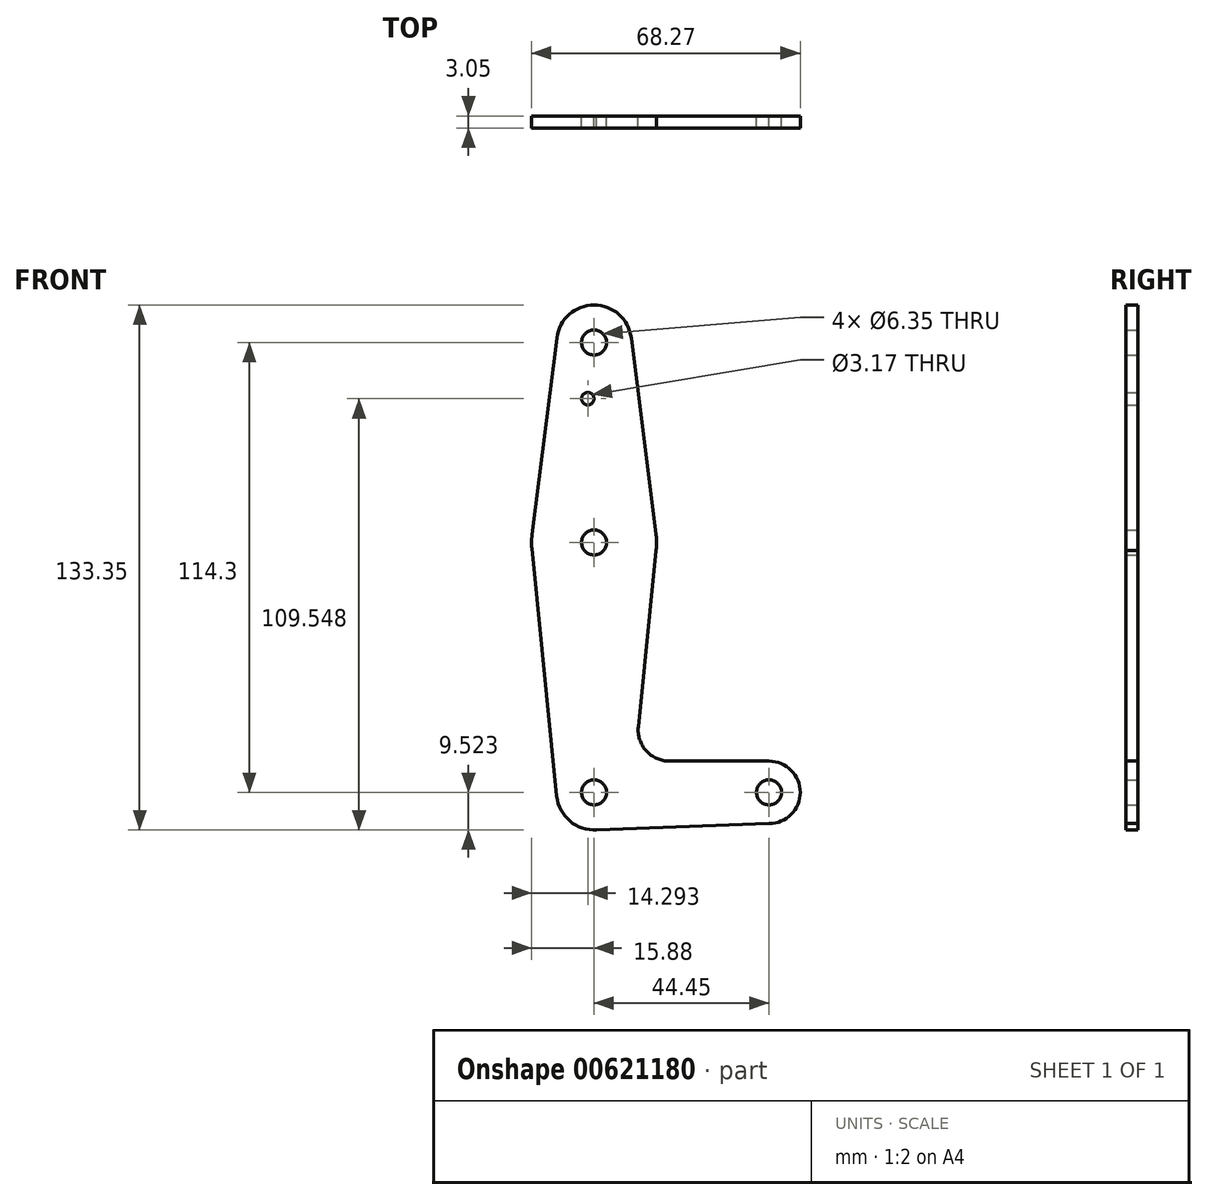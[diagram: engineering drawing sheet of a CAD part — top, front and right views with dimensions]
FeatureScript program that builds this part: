
annotation { "Feature Type Name" : "Feature", "Feature Type Description" : "" }
export const myFeature = defineFeature(function(context is Context, id is Id, definition is map)
    precondition{}
    {
        {
            var Q0;
            Q0=qCreatedBy(makeId("Front.planeOp"),FACE);
            var sketch = newSketch(context, id + "F0", { "sketchPlane" : qUnion([Q0])});
            skCircle(sketch, "E0", {"center": v(0, 85.95) * mm, "radius": 9.53 * mm});
            skCircle(sketch, "E1", {"center": v(0, 35.15) * mm, "radius": 15.88 * mm});
            skCircle(sketch, "E2", {"center": v(0, -28.35) * mm, "radius": 9.53 * mm});
            skCircle(sketch, "E3", {"center": v(44.45, -28.35) * mm, "radius": 7.94 * mm});
            skLineSegment(sketch, "E4", {"start": v(-9.45, 87.14) * mm, "end": v(-15.75, 37.14) * mm});
            skLineSegment(sketch, "E5", {"start": v(15.75, 37.14) * mm, "end": v(9.45, 87.14) * mm});
            skLineSegment(sketch, "E6", {"start": v(15.75, 33.17) * mm, "end": v(11.24, -11.66) * mm});
            skLineSegment(sketch, "E7", {"start": v(19.16, -20.4) * mm, "end": v(44.45, -20.4) * mm});
            skLineSegment(sketch, "E8", {"start": v(0, -37.87) * mm, "end": v(44.45, -36.28) * mm});
            skCircle(sketch, "E9", {"center": v(0, 85.95) * mm, "radius": 3.18 * mm});
            skCircle(sketch, "E10", {"center": v(-1.59, 71.68) * mm, "radius": 1.59 * mm});
            skCircle(sketch, "E11", {"center": v(0, 35.15) * mm, "radius": 3.18 * mm});
            skCircle(sketch, "E12", {"center": v(0, -28.35) * mm, "radius": 3.18 * mm});
            skCircle(sketch, "E13", {"center": v(44.45, -28.35) * mm, "radius": 3.18 * mm});
            skPoint(sketch, "E14.newPointB", {"position": v(9.57, -28.35) * mm});
            skArc(sketch, "E14.filletArc", {"start": v(11.24, -11.66) * mm, "mid": v(13.26, -17.8) * mm, "end": v(19.16, -20.4) * mm});
            skLineSegment(sketch, "E15", {"start": v(0, 85.95) * mm, "end": v(0, 35.15) * mm});
            skLineSegment(sketch, "E16", {"start": v(0, 35.15) * mm, "end": v(0, -18.82) * mm});
            skLineSegment(sketch, "E17", {"start": v(-15.8, 33.57) * mm, "end": v(-9.48, -29.3) * mm});
            skSolve(sketch);
        }
        {
            var Q0;
            Q0 = qSketchRegion(id + "F0", true);
            extrude(context, id + "F1", {"entities" : qUnion([Q0]), "depth" : 3.05 * mm, "offsetDistance" : 25.4 * mm});
        }
    });
